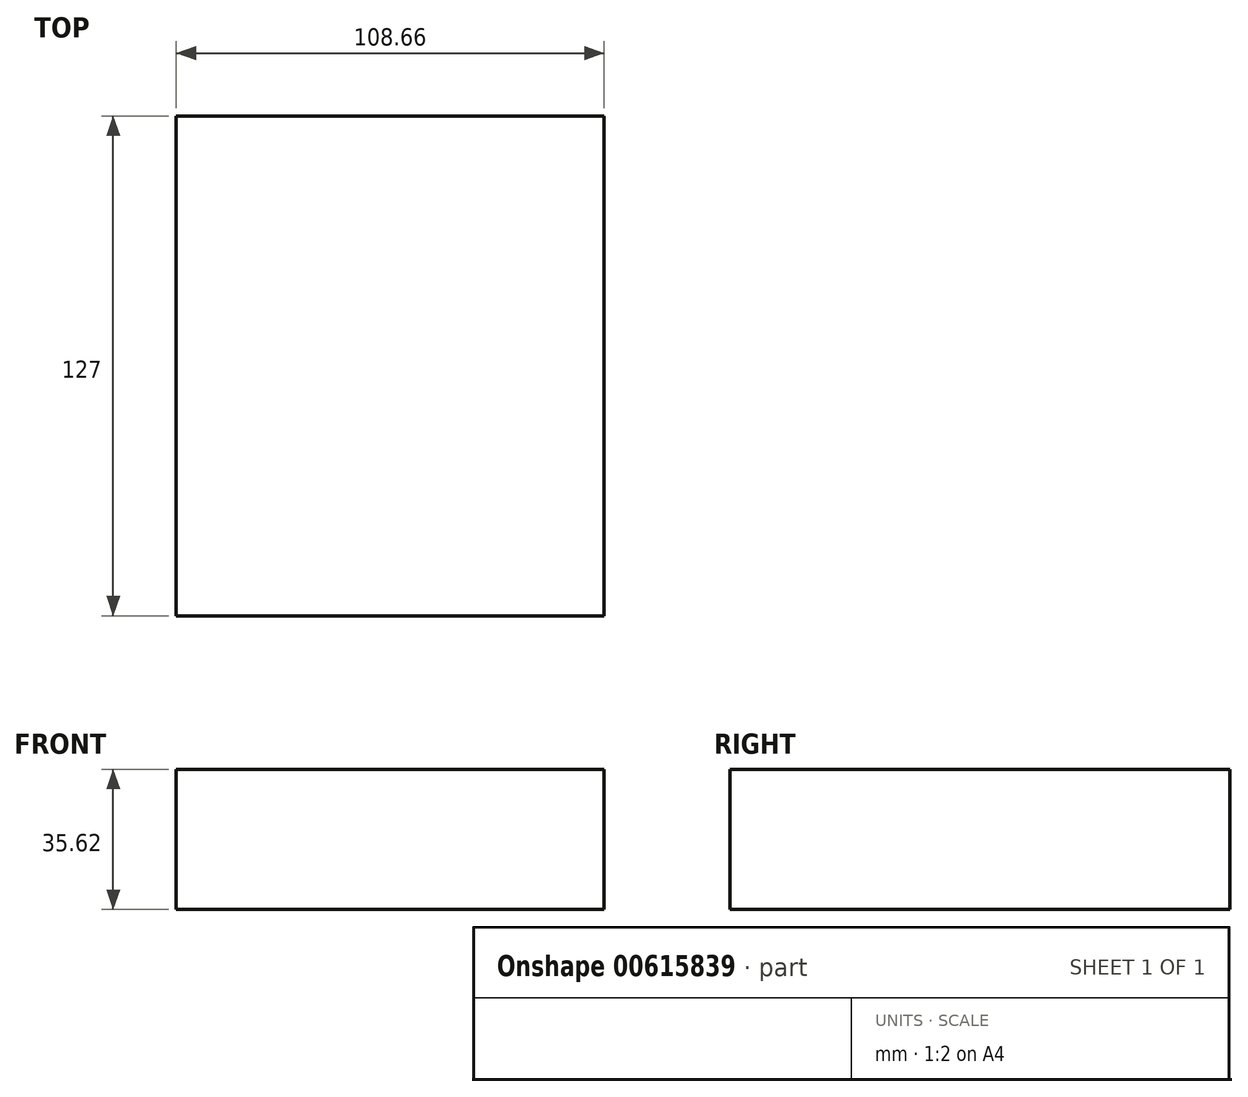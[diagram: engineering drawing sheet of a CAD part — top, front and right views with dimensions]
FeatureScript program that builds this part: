
annotation { "Feature Type Name" : "Feature", "Feature Type Description" : "" }
export const myFeature = defineFeature(function(context is Context, id is Id, definition is map)
    precondition{}
    {
        {
            var Q0;
            Q0=qCreatedBy(makeId("Front.planeOp"),FACE);
            var sketch = newSketch(context, id + "F0", { "sketchPlane" : qUnion([Q0])});
            skLineSegment(sketch, "E0.bottom", {"start": v(-45.94, 37.81) * mm, "end": v(62.72, 37.81) * mm});
            skLineSegment(sketch, "E0.top", {"start": v(-45.94, 2.2) * mm, "end": v(62.72, 2.2) * mm});
            skLineSegment(sketch, "E0.left", {"start": v(-45.94, 37.81) * mm, "end": v(-45.94, 2.2) * mm});
            skLineSegment(sketch, "E0.right", {"start": v(62.72, 37.81) * mm, "end": v(62.72, 2.2) * mm});
            skSolve(sketch);
        }
        {
            var Q0;
            Q0=makeQuery(id+"F0.imprint","IMPRINT",FACE,{"disambiguationData":[TD([[makeQuery(id+"F0.imprint","IMPRINT",EDGE,{"derivedFrom":sQuery(id+"F0.wireOp",EDGE,"E0.bottom")}),-1.0]])]});
            extrude(context, id + "F1", {"entities" : qUnion([Q0]), "oppositeDirection" : true, "depth" : 127 * mm, "offsetDistance" : 25.4 * mm});
        }
    });
